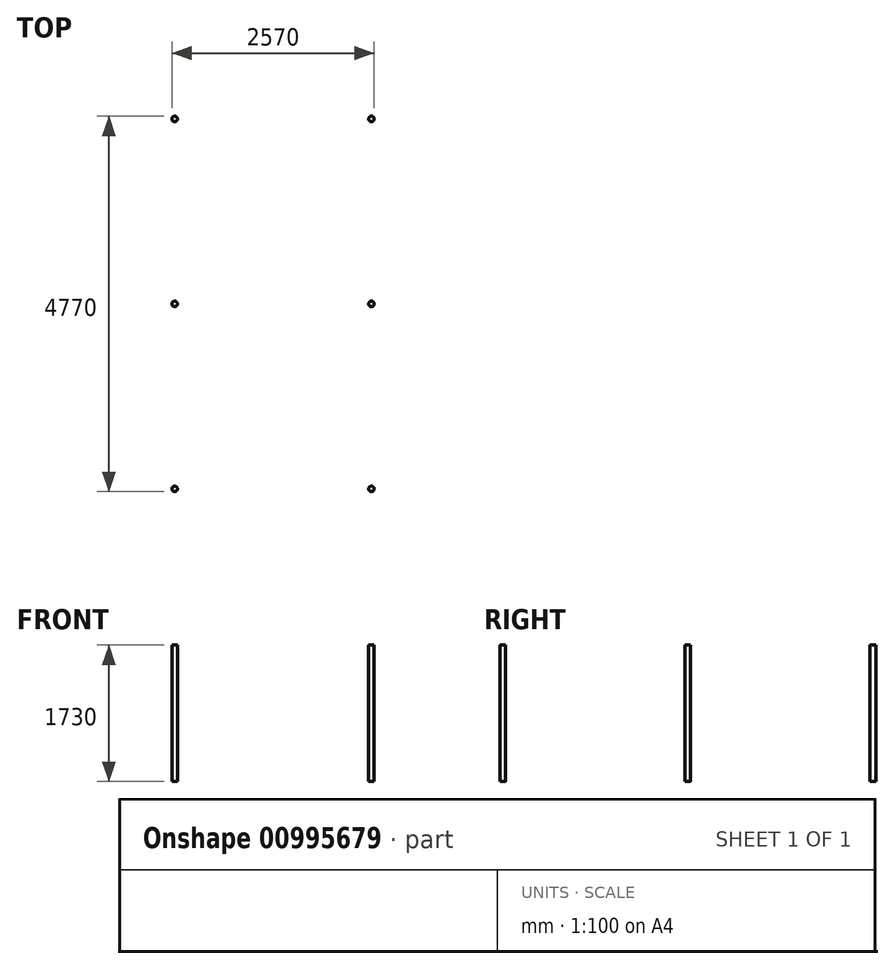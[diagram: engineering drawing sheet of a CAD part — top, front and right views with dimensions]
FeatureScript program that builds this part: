
annotation { "Feature Type Name" : "Feature", "Feature Type Description" : "" }
export const myFeature = defineFeature(function(context is Context, id is Id, definition is map)
    precondition{}
    {
        {
            var Q0;
            Q0=qCreatedBy(makeId("Top.planeOp"),FACE);
            var sketch = newSketch(context, id + "F0", { "sketchPlane" : qUnion([Q0])});
            skLineSegment(sketch, "E0.bottom", {"start": v(-1250, -2500) * mm, "end": v(1250, -2500) * mm, "construction": true});
            skLineSegment(sketch, "E0.top", {"start": v(-1250, 2500) * mm, "end": v(1250, 2500) * mm, "construction": true});
            skLineSegment(sketch, "E0.left", {"start": v(-1250, -2500) * mm, "end": v(-1250, 2500) * mm, "construction": true});
            skLineSegment(sketch, "E0.right", {"start": v(1250, -2500) * mm, "end": v(1250, 2500) * mm, "construction": true});
            skPoint(sketch, "E0.middle", {"position": v(0, 0) * mm});
            skLineSegment(sketch, "E1", {"start": v(-1250, 2350) * mm, "end": v(1250, 2350) * mm, "construction": true});
            skLineSegment(sketch, "E2", {"start": v(-1250, 0) * mm, "end": v(1250, 0) * mm, "construction": true});
            skLineSegment(sketch, "E3", {"start": v(-1250, -2350) * mm, "end": v(1250, -2350) * mm, "construction": true});
            skCircle(sketch, "E4", {"center": v(-1250, 2350) * mm, "radius": 35 * mm});
            skCircle(sketch, "E5", {"center": v(-1250, 0) * mm, "radius": 35 * mm});
            skCircle(sketch, "E6", {"center": v(-1250, -2350) * mm, "radius": 35 * mm});
            skLineSegment(sketch, "E7", {"start": v(0, 2500) * mm, "end": v(0, -2500) * mm, "construction": true});
            skCircle(sketch, "E8", {"center": v(1250, -2350) * mm, "radius": 35 * mm});
            skCircle(sketch, "E9", {"center": v(1250, 2350) * mm, "radius": 35 * mm});
            skCircle(sketch, "E10", {"center": v(1250, 0) * mm, "radius": 35 * mm});
            skSolve(sketch);
        }
        {
            var Q0;
            Q0=makeQuery(id+"F0.imprint","IMPRINT",FACE,{"disambiguationData":[TD([[makeQuery(id+"F0.imprint","IMPRINT",EDGE,{"derivedFrom":sQuery(id+"F0.wireOp",EDGE,"E8")}),1.0]])]});
            var Q1;
            Q1=makeQuery(id+"F0.imprint","IMPRINT",FACE,{"disambiguationData":[TD([[makeQuery(id+"F0.imprint","IMPRINT",EDGE,{"derivedFrom":sQuery(id+"F0.wireOp",EDGE,"E6")}),1.0]])]});
            var Q2;
            Q2=makeQuery(id+"F0.imprint","IMPRINT",FACE,{"disambiguationData":[TD([[makeQuery(id+"F0.imprint","IMPRINT",EDGE,{"derivedFrom":sQuery(id+"F0.wireOp",EDGE,"E10")}),1.0]])]});
            var Q3;
            Q3=makeQuery(id+"F0.imprint","IMPRINT",FACE,{"disambiguationData":[TD([[makeQuery(id+"F0.imprint","IMPRINT",EDGE,{"derivedFrom":sQuery(id+"F0.wireOp",EDGE,"E9")}),1.0]])]});
            var Q4;
            Q4=makeQuery(id+"F0.imprint","IMPRINT",FACE,{"disambiguationData":[TD([[makeQuery(id+"F0.imprint","IMPRINT",EDGE,{"derivedFrom":sQuery(id+"F0.wireOp",EDGE,"E5")}),1.0]])]});
            var Q5;
            Q5=makeQuery(id+"F0.imprint","IMPRINT",FACE,{"disambiguationData":[TD([[makeQuery(id+"F0.imprint","IMPRINT",EDGE,{"derivedFrom":sQuery(id+"F0.wireOp",EDGE,"E4")}),1.0]])]});
            extrude(context, id + "F1", {"entities" : qUnion([Q0, Q1, Q2, Q3, Q4, Q5]), "depth" : 1730 * mm, "offsetDistance" : 25 * mm});
        }
    });
